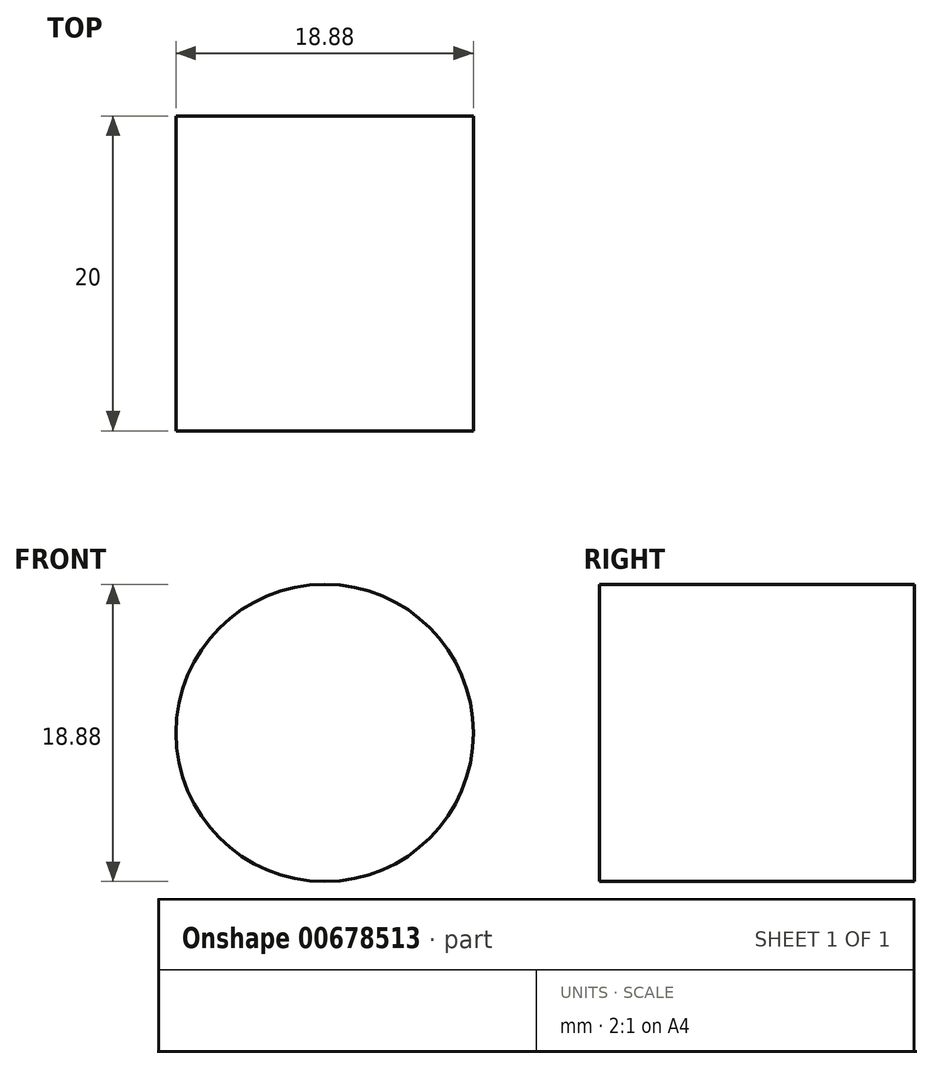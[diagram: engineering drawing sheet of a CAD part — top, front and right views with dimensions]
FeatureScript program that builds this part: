
annotation { "Feature Type Name" : "Feature", "Feature Type Description" : "" }
export const myFeature = defineFeature(function(context is Context, id is Id, definition is map)
    precondition{}
    {
        {
            var Q0;
            Q0=qCreatedBy(makeId("Front.planeOp"),FACE);
            var sketch = newSketch(context, id + "F0", { "sketchPlane" : qUnion([Q0])});
            skCircle(sketch, "E0", {"center": v(0, 0) * mm, "radius": 9.44 * mm});
            skSolve(sketch);
        }
        {
            var Q0;
            Q0=makeQuery(id+"F0.imprint","IMPRINT",FACE,{"disambiguationData":[TD([[makeQuery(id+"F0.imprint","IMPRINT",EDGE,{"derivedFrom":sQuery(id+"F0.wireOp",EDGE,"E0")}),1.0]])]});
            extrude(context, id + "F1", {"entities" : qUnion([Q0]), "depth" : 20 * mm, "offsetDistance" : 25 * mm});
        }
    });
